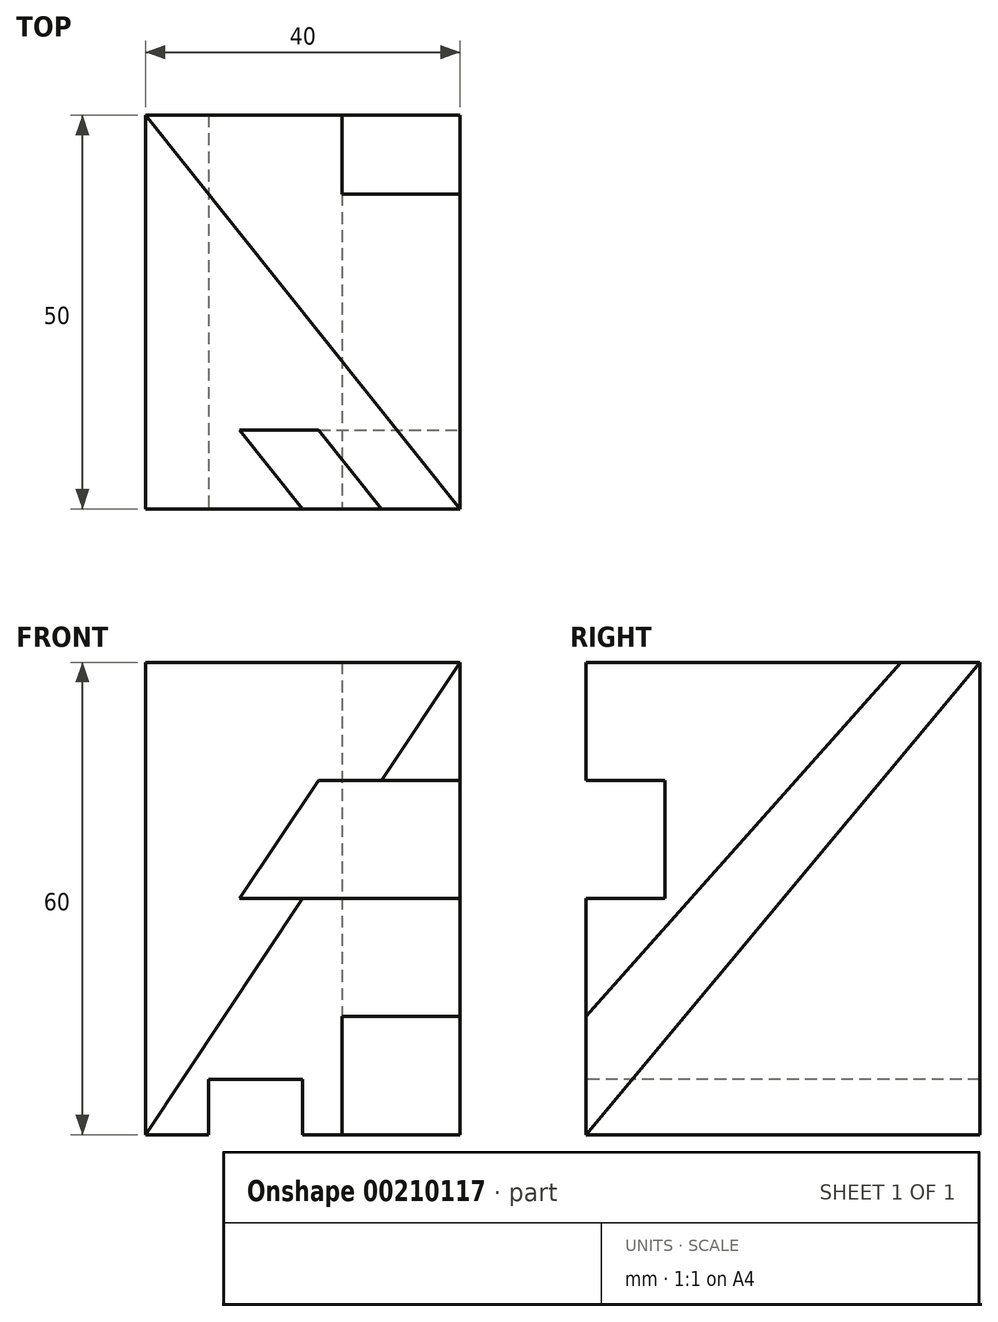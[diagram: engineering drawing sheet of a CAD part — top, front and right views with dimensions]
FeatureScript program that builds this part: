
annotation { "Feature Type Name" : "Feature", "Feature Type Description" : "" }
export const myFeature = defineFeature(function(context is Context, id is Id, definition is map)
    precondition{}
    {
        {
            var Q0;
            Q0=qCreatedBy(makeId("Front.planeOp"),FACE);
            var sketch = newSketch(context, id + "F0", { "sketchPlane" : qUnion([Q0])});
            skLineSegment(sketch, "E0.bottom", {"start": v(0, 0) * mm, "end": v(40, 0) * mm});
            skLineSegment(sketch, "E0.top", {"start": v(0, 60) * mm, "end": v(40, 60) * mm});
            skLineSegment(sketch, "E0.left", {"start": v(0, 0) * mm, "end": v(0, 60) * mm});
            skLineSegment(sketch, "E0.right", {"start": v(40, 0) * mm, "end": v(40, 60) * mm});
            skSolve(sketch);
        }
        {
            var Q0;
            Q0 = qSketchRegion(id + "F0", true);
            extrude(context, id + "F1", {"entities" : qUnion([Q0]), "oppositeDirection" : true, "depth" : 50 * mm});
        }
        {
            var Q0;
            Q0=makeQuery(id+"F1.opExtrude","SWEPT_FACE",FACE,{"disambiguationData":[OSD([sQuery(id+"F0.wireOp",EDGE,"E0.right")])]});
            var sketch = newSketch(context, id + "F2", { "sketchPlane" : qUnion([Q0])});
            skLineSegment(sketch, "E1", {"start": v(0, 0) * mm, "end": v(0, 15) * mm});
            skLineSegment(sketch, "E2", {"start": v(0, 15) * mm, "end": v(40, 60) * mm});
            skLineSegment(sketch, "E3", {"start": v(40, 60) * mm, "end": v(50, 60) * mm});
            skLineSegment(sketch, "E4", {"start": v(50, 60) * mm, "end": v(0, 0) * mm});
            skSolve(sketch);
        }
        {
            var Q0;
            Q0=qCreatedBy(makeId("Right.planeOp"),FACE);
            cPlane(context, id + "F3", {"entities" : qUnion([Q0]), "cplaneType" : CPlaneType.OFFSET, "offset" : 25 * mm, "width" : 150 * mm, "height" : 150 * mm});
        }
        {
            var Q0;
            Q0 = qSketchRegion(id + "F2", true);
            var Q1;
            Q1=qCreatedBy(id+"F3.planeOp",FACE);
            extrude(context, id + "F4", {"entities" : qUnion([Q0]), "operationType" : NewBodyOperationType.REMOVE, "endBound" : BoundingType.UP_TO_SURFACE, "oppositeDirection" : true, "endBoundEntityFace" : qUnion([Q1]), "depth" : 25 * mm});
        }
        {
            var Q0;
            Q0=makeQuery(id+"F4CNHB0jdq8woxA_1.splitOp","SPLIT",FACE,{"derivedFrom":makeQuery(id+"F1.opExtrude","CAP_FACE",FACE,{"disambiguationData":[OSD([sQuery(id+"F0.wireOp",EDGE,"E0.bottom"),sQuery(id+"F0.wireOp",EDGE,"E0.top"),sQuery(id+"F0.wireOp",EDGE,"E0.left"),sQuery(id+"F0.wireOp",EDGE,"E0.right")])],"isStart":true}),"isFromBackBody":true});
            var sketch = newSketch(context, id + "F5", { "sketchPlane" : qUnion([Q0])});
            skLineSegment(sketch, "E5.bottom", {"start": v(8, 0) * mm, "end": v(20, 0) * mm});
            skLineSegment(sketch, "E5.top", {"start": v(8, 7) * mm, "end": v(20, 7) * mm});
            skLineSegment(sketch, "E5.left", {"start": v(8, 0) * mm, "end": v(8, 7) * mm});
            skLineSegment(sketch, "E5.right", {"start": v(20, 0) * mm, "end": v(20, 7) * mm});
            skSolve(sketch);
        }
        {
            var Q0;
            Q0 = qSketchRegion(id + "F5", true);
            extrude(context, id + "F6", {"entities" : qUnion([Q0]), "operationType" : NewBodyOperationType.REMOVE, "endBound" : BoundingType.THROUGH_ALL, "oppositeDirection" : true, "depth" : 25 * mm});
        }
        {
            var Q0;
            {var subQ0=sQuery(id+"F0.wireOp",EDGE,"E0.right");var subQ2=sQuery(id+"F0.wireOp",EDGE,"E0.top");var subQ4=makeQuery(id+"F1.opExtrude","SWEPT_FACE",FACE,{"disambiguationData":[OSD([subQ2])]});Q0=makeQuery(id+"F4.boolean.opBoolean","SPLIT",FACE,{"disambiguationData":[TD([subQ4])],"derivedFrom":makeQuery(id+"F1.opExtrude","SWEPT_FACE",FACE,{"disambiguationData":[OSD([subQ0])]})});}
            var sketch = newSketch(context, id + "F7", { "sketchPlane" : qUnion([Q0])});
            skLineSegment(sketch, "E6.bottom", {"start": v(0, 45) * mm, "end": v(10, 45) * mm});
            skLineSegment(sketch, "E6.top", {"start": v(0, 30) * mm, "end": v(10, 30) * mm});
            skLineSegment(sketch, "E6.left", {"start": v(0, 45) * mm, "end": v(0, 30) * mm});
            skLineSegment(sketch, "E6.right", {"start": v(10, 45) * mm, "end": v(10, 30) * mm});
            skSolve(sketch);
        }
        {
            var Q0;
            Q0 = qSketchRegion(id + "F7", true);
            extrude(context, id + "F8", {"entities" : qUnion([Q0]), "operationType" : NewBodyOperationType.REMOVE, "endBound" : BoundingType.THROUGH_ALL, "oppositeDirection" : true, "depth" : 25 * mm});
        }
        {
            var Q0;
            Q0=makeQuery(id+"F1.opExtrude","SWEPT_FACE",FACE,{"disambiguationData":[OSD([sQuery(id+"F0.wireOp",EDGE,"E0.top")])]});
            var sketch = newSketch(context, id + "F9", { "sketchPlane" : qUnion([Q0])});
            skLineSegment(sketch, "E7", {"start": v(0, 50) * mm, "end": v(0, 0) * mm});
            skLineSegment(sketch, "E8", {"start": v(0, 0) * mm, "end": v(40, 0) * mm});
            skLineSegment(sketch, "E9", {"start": v(40, 0) * mm, "end": v(0, 50) * mm});
            skSolve(sketch);
        }
        {
            var Q1;
            Q1=makeQuery(id+"F9.imprint","IMPRINT",FACE,{"disambiguationData":[TD([[makeQuery(id+"F9.imprint","IMPRINT",EDGE,{"derivedFrom":sQuery(id+"F9.wireOp",EDGE,"E7")}),1.0]])]});
            var Q2;
            Q2=qCreatedBy(makeId("Origin.pointOp"),VERTEX);
            loft(context, id + "F10", {"operationType" : NewBodyOperationType.REMOVE, "sheetProfilesArray" : [{ "sheetProfileEntities" : qUnion([Q1]) }, { "sheetProfileEntities" : qUnion([Q2]) }]});
        }
    });
